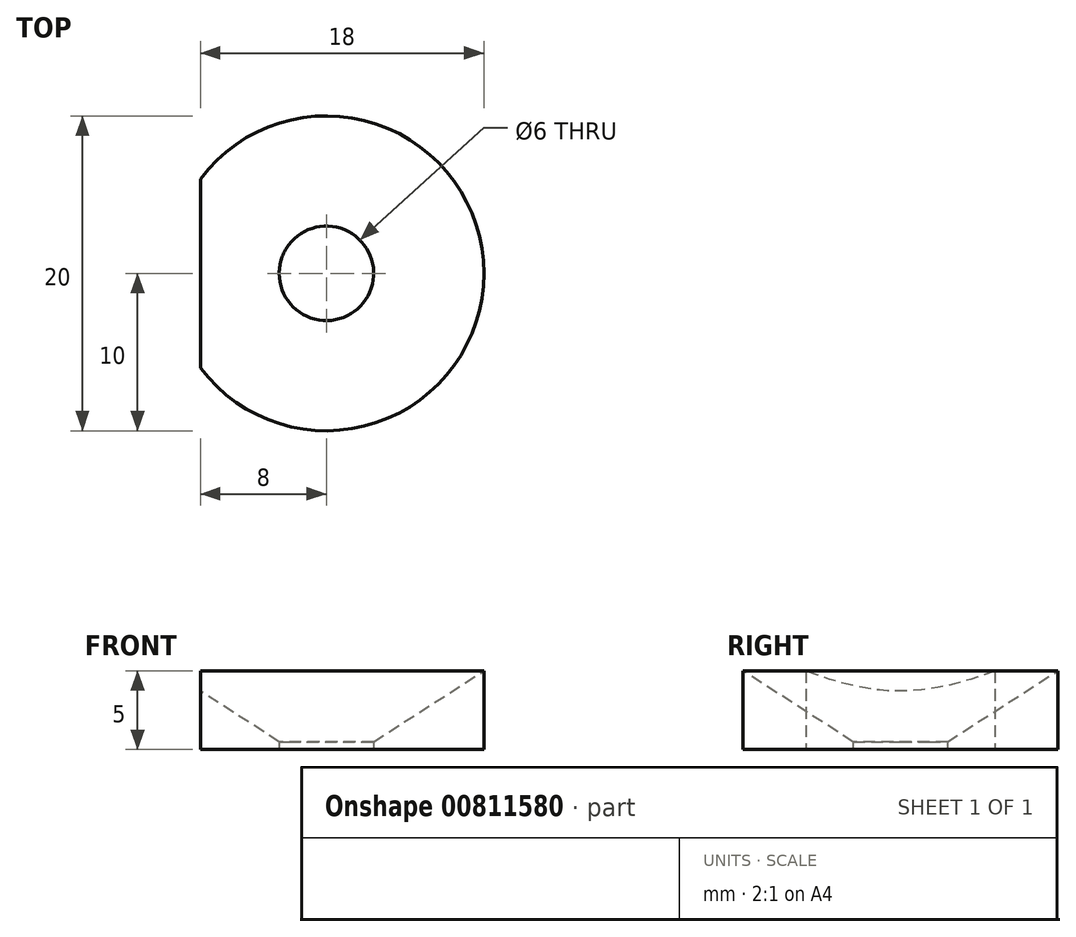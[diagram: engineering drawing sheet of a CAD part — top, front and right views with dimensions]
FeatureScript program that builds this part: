
annotation { "Feature Type Name" : "Feature", "Feature Type Description" : "" }
export const myFeature = defineFeature(function(context is Context, id is Id, definition is map)
    precondition{}
    {
        {
            var Q0;
            Q0=qCreatedBy(makeId("Front.planeOp"),FACE);
            var sketch = newSketch(context, id + "F0", { "sketchPlane" : qUnion([Q0])});
            skLineSegment(sketch, "E0", {"start": v(0, 0) * mm, "end": v(-10, 0) * mm});
            skLineSegment(sketch, "E1", {"start": v(-10, 0) * mm, "end": v(-10, 5) * mm});
            skLineSegment(sketch, "E2", {"start": v(-10, 5) * mm, "end": v(-3, 0.5) * mm});
            skLineSegment(sketch, "E3", {"start": v(-3, 0.5) * mm, "end": v(-3, 0) * mm});
            skLineSegment(sketch, "E4", {"start": v(0, -5.5) * mm, "end": v(0, 9.25) * mm, "construction": true});
            skSolve(sketch);
        }
        {
            var Q0;
            Q0 = qSketchRegion(id + "F0", true);
            var Q1;
            Q1=sQuery(id+"F0.wireOp",EDGE,"E4");
            revolve(context, id + "F1", {"surfaceOperationType" : NewSurfaceOperationType.NEW, "entities" : qUnion([Q0]), "axis" : qUnion([Q1]), "revolveType" : RevolveType.FULL});
        }
        {
            var Q0;
            Q0=makeQuery(id+"F1.opRevolve","SWEPT_FACE",FACE,{"disambiguationData":[OSD([sQuery(id+"F0.wireOp",EDGE,"E0")])]});
            var sketch = newSketch(context, id + "F2", { "sketchPlane" : qUnion([Q0])});
            skLineSegment(sketch, "E5", {"start": v(-8, 6) * mm, "end": v(-8, -6) * mm});
            skSolve(sketch);
        }
        {
            var Q0;
            {var subQ0=sQuery(id+"F2.wireOp",EDGE,"E5");Q0=makeQuery(id+"F2.imprint","IMPRINT",FACE,{"disambiguationData":[TD([[makeQuery(id+"F2.imprint","IMPRINT",EDGE,{"derivedFrom":subQ0}),-1.0]])]});}
            extrude(context, id + "F3", {"entities" : qUnion([Q0]), "operationType" : NewBodyOperationType.REMOVE, "oppositeDirection" : true, "depth" : 25 * mm, "offsetDistance" : 25 * mm});
        }
    });
